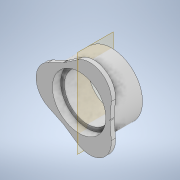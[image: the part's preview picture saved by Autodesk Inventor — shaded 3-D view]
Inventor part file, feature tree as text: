
AUTODESK INVENTOR PART (.ipt)
format: ipt  version: 2020 (Build 240168000, 168)  size: 183,296 bytes
history: native  units: in
note: dims shown in document units (in); Inventor stores cm internally (conversion verified against a paired STEP export)
features: projected_geometry x5, sketch x4, extrude x2, revolve x2
ambient origin geometry x8: Origin, YZ Plane, XZ Plane, XY Plane, X Axis, Y Axis, Z Axis, Center Point
bodies: Solid1 (feature_tree)
feature tree (13):
  extrude  "Extrusion1"  Depth=4.0551in
  revolve  "Revolution1"  [1 undecoded]
  revolve  "Revolution2"  Angle=90.0deg
  extrude  "Extrusion2"  TaperAngle=90.0deg  [1 undecoded]
  sketch  "Sketch1"  dims[d0=2.1713in d1=4.0551in]
  sketch  "Sketch2"  dims[d2=1.5354in d3=0.0in d4=0.3937in]
  projected_geometry  "Projected Loop1"
  projected_geometry  "Projected Loop2"
  sketch  "Sketch3"  dims[d5=1.2598in d6=90.0deg]
  sketch  "Sketch4"  dims[d7=0.1969in d9=90.0deg d11=0.1969in d12=120.0deg d13=120.0deg d14=120.0deg d15=120.0deg d16=0.3937in d17=0.0in]
  projected_geometry  "Projected Loop3"
  projected_geometry  "Project Cut Edges1"
  projected_geometry  "Project Cut Edges2"
note: 2 required parameter values undecoded (feature->parameter linkage not recoverable at this tier; creation-order binding heuristic only, values carry confidence <= 0.55)